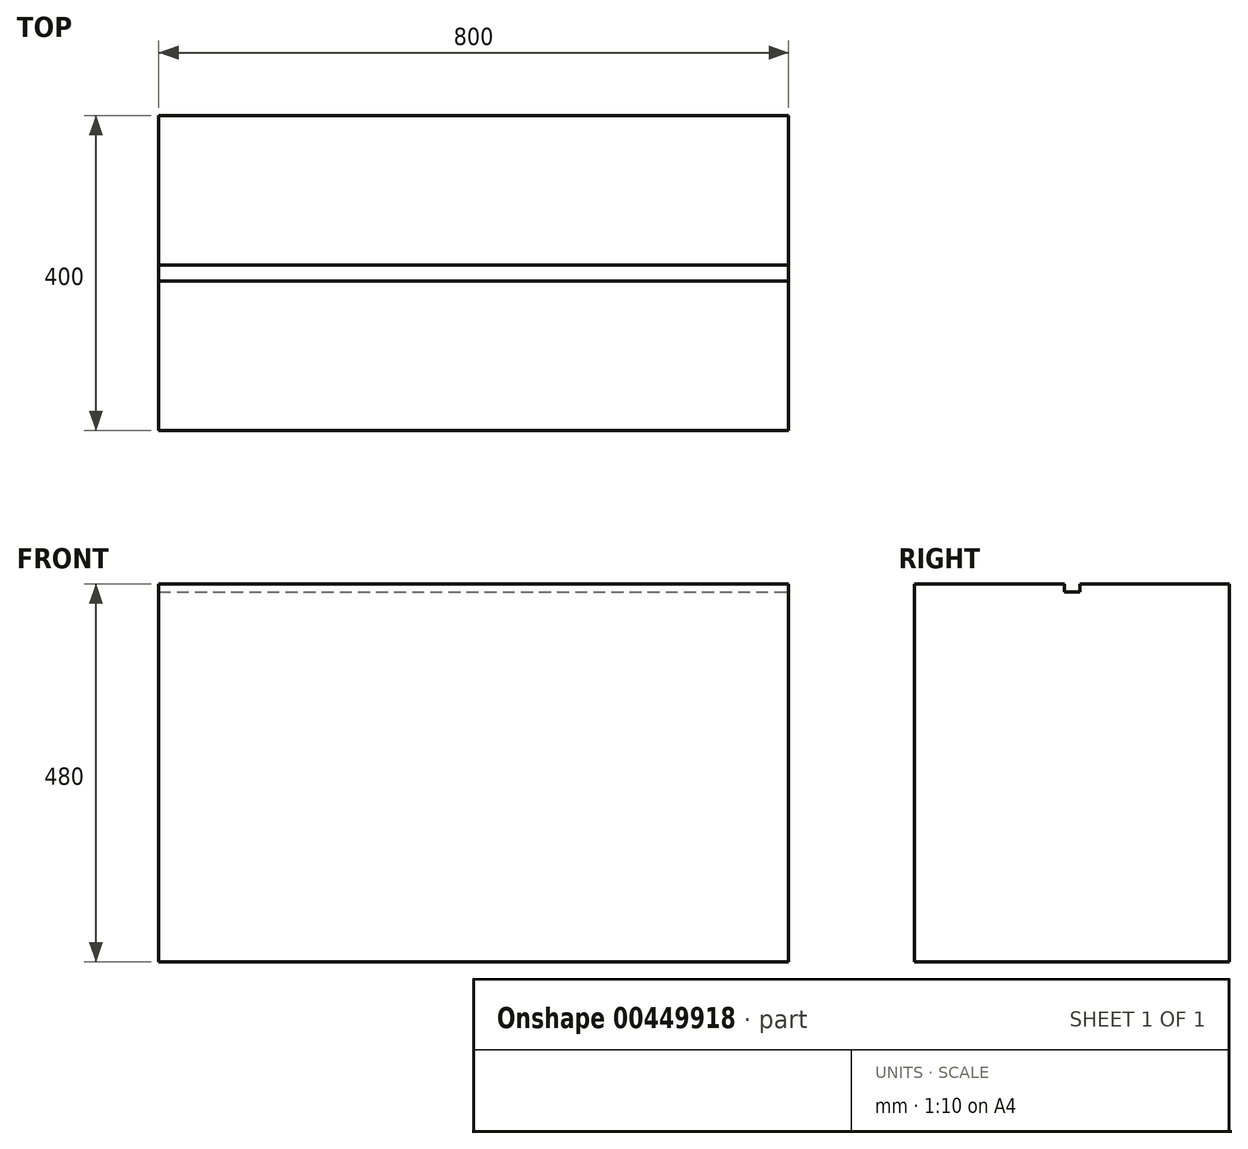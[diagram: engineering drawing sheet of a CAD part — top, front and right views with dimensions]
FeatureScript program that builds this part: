
annotation { "Feature Type Name" : "Feature", "Feature Type Description" : "" }
export const myFeature = defineFeature(function(context is Context, id is Id, definition is map)
    precondition{}
    {
        {
            var Q0;
            Q0=qCreatedBy(makeId("Right.planeOp"),FACE);
            var sketch = newSketch(context, id + "F0", { "sketchPlane" : qUnion([Q0])});
            skLineSegment(sketch, "E0.bottom", {"start": v(-160.6, 343.56) * mm, "end": v(239.4, 343.56) * mm});
            skLineSegment(sketch, "E0.top", {"start": v(-160.6, -136.44) * mm, "end": v(239.4, -136.44) * mm});
            skLineSegment(sketch, "E0.left", {"start": v(-160.6, 343.56) * mm, "end": v(-160.6, -136.44) * mm});
            skLineSegment(sketch, "E0.right", {"start": v(239.4, 343.56) * mm, "end": v(239.4, -136.44) * mm});
            skSolve(sketch);
        }
        {
            var Q0;
            Q0=qSketchRegion(id+"F0",true);
            extrude(context, id + "F1", {"entities" : qUnion([Q0]), "flatOperationType" : FlatOperationType.REMOVE, "oppositeDirection" : true, "offsetDistance" : 25 * mm, "depth" : 800 * mm, "domain" : OperationDomain.MODEL});
        }
        {
            var Q0;
            Q0=makeQuery(id+"F1.opExtrude","CAP_FACE",FACE,{"disambiguationData":[OSD([sQuery(id+"F0.wireOp",EDGE,"E0.bottom"),sQuery(id+"F0.wireOp",EDGE,"E0.top"),sQuery(id+"F0.wireOp",EDGE,"E0.left"),sQuery(id+"F0.wireOp",EDGE,"E0.right")])],"isStart":true});
            var sketch = newSketch(context, id + "F2", { "sketchPlane" : qUnion([Q0])});
            skLineSegment(sketch, "E1.bottom", {"start": v(29.4, 343.56) * mm, "end": v(49.4, 343.56) * mm});
            skLineSegment(sketch, "E1.top", {"start": v(29.4, 333.56) * mm, "end": v(49.4, 333.56) * mm});
            skLineSegment(sketch, "E1.left", {"start": v(29.4, 343.56) * mm, "end": v(29.4, 333.56) * mm});
            skLineSegment(sketch, "E1.right", {"start": v(49.4, 343.56) * mm, "end": v(49.4, 333.56) * mm});
            skLineSegment(sketch, "E2.top", {"start": v(39.4, 343.56) * mm, "end": v(93.02, 343.56) * mm});
            skLineSegment(sketch, "E2.left", {"start": v(39.4, 343.56) * mm, "end": v(39.4, 343.56) * mm});
            skLineSegment(sketch, "E2.right", {"start": v(93.02, 332.94) * mm, "end": v(93.02, 343.56) * mm});
            skSolve(sketch);
        }
        {
            var Q0;
            Q0=qSketchRegion(id+"F2",true);
            extrude(context, id + "F3", {"entities" : qUnion([Q0]), "operationType" : NewBodyOperationType.REMOVE, "flatOperationType" : FlatOperationType.REMOVE, "oppositeDirection" : true, "offsetDistance" : 25 * mm, "depth" : 800 * mm, "domain" : OperationDomain.MODEL});
        }
    });
